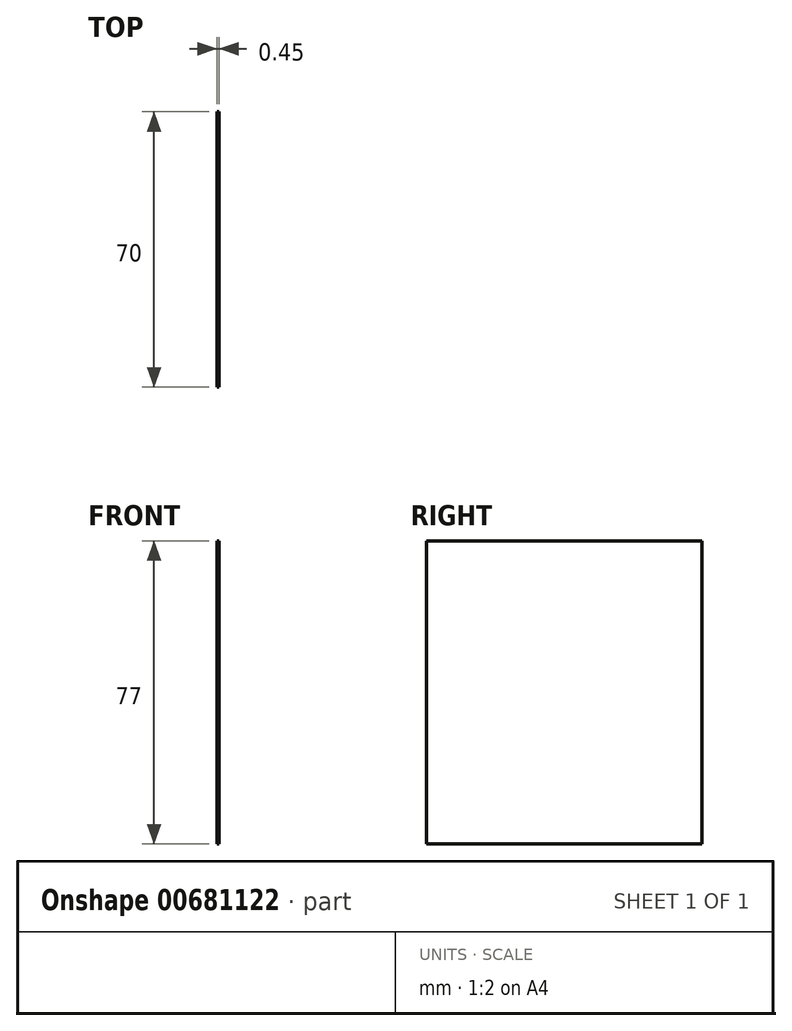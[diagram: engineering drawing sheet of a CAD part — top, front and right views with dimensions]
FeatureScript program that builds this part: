
annotation { "Feature Type Name" : "Feature", "Feature Type Description" : "" }
export const myFeature = defineFeature(function(context is Context, id is Id, definition is map)
    precondition{}
    {
        {
            var Q0;
            Q0=qCreatedBy(makeId("Right.planeOp"),FACE);
            var sketch = newSketch(context, id + "F0", { "sketchPlane" : qUnion([Q0])});
            skLineSegment(sketch, "E0.bottom", {"start": v(0, 0) * mm, "end": v(70, 0) * mm});
            skLineSegment(sketch, "E0.top", {"start": v(0, -77) * mm, "end": v(70, -77) * mm});
            skLineSegment(sketch, "E0.left", {"start": v(0, 0) * mm, "end": v(0, -77) * mm});
            skLineSegment(sketch, "E0.right", {"start": v(70, 0) * mm, "end": v(70, -77) * mm});
            skSolve(sketch);
        }
        {
            var Q0;
            Q0=makeQuery(id+"F0.imprint","IMPRINT",FACE,{"disambiguationData":[TD([[makeQuery(id+"F0.imprint","IMPRINT",EDGE,{"derivedFrom":sQuery(id+"F0.wireOp",EDGE,"E0.bottom")}),-1.0]])]});
            extrude(context, id + "F1", {"entities" : qUnion([Q0]), "depth" : .45 * mm, "offsetDistance" : 25 * mm});
        }
    });
